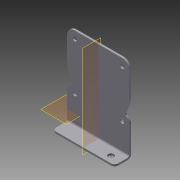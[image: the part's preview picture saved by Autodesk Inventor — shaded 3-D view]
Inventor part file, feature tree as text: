
AUTODESK INVENTOR PART (.ipt)
format: ipt  version: 2014 (Build 180170000, 170)  size: 171,008 bytes
history: native  units: in
note: dims shown in document units (in); Inventor stores cm internally (conversion verified against a paired STEP export)
features: sketch x6, extrude x4, fillet x3, hole x2, reference x2, plane x1, mirror x1
ambient origin geometry x8: Origin, YZ Plane, XZ Plane, XY Plane, X Axis, Y Axis, Z Axis, Center Point
bodies: Solid1 (feature_tree)
feature tree (19):
  extrude  "Extrusion1"  Depth=2.11in
  extrude  "Extrusion5"  Depth=2.11in
  extrude  "Extrusion2"  Depth=0.5in TaperAngle=0.0deg
  extrude  "Extrusion4"  Depth=0.25in TaperAngle=0.0deg
  hole  "Hole3"  [1 undecoded]
  plane  "Work Plane1"
  fillet  "Fillet3"  Radius=0.063in
  fillet  "Fillet4"  Radius=0.125in
  fillet  "Fillet5"  Radius=0.125in
  hole  "Hole6"  [1 undecoded]
  mirror  "Mirror1"
  sketch  "Sketch1"  dims[d0=2.11in d1=2.5in]
  sketch  "Sketch2"  dims[d2=0.0625in d3=0.0in d4=2.11in]
  sketch  "Sketch6"  dims[d6=0.5in d7=0.0in d29=1.0in d30=0.0in]
  reference  "Reference2"
  sketch  "Sketch7"  dims[d31=0.15in d32=0.75in d33=0.279in d34=0.25in d35=0.5635in d36=1.0in d37=0.8108in d57=1.0in d58=0.0in]
  sketch  "Sketch9"  dims[d59=0.063in d60=2.856in d61=0.063in d62=0.125in d63=0.125in]
  sketch  "Sketch10"  dims[d64=0.201in d65=0.75in d66=0.385in d67=0.25in d68=0.5635in d69=1.0in d70=0.8108in]
  reference  "Reference3"
note: 2 required parameter values undecoded (feature->parameter linkage not recoverable at this tier; creation-order binding heuristic only, values carry confidence <= 0.55)
